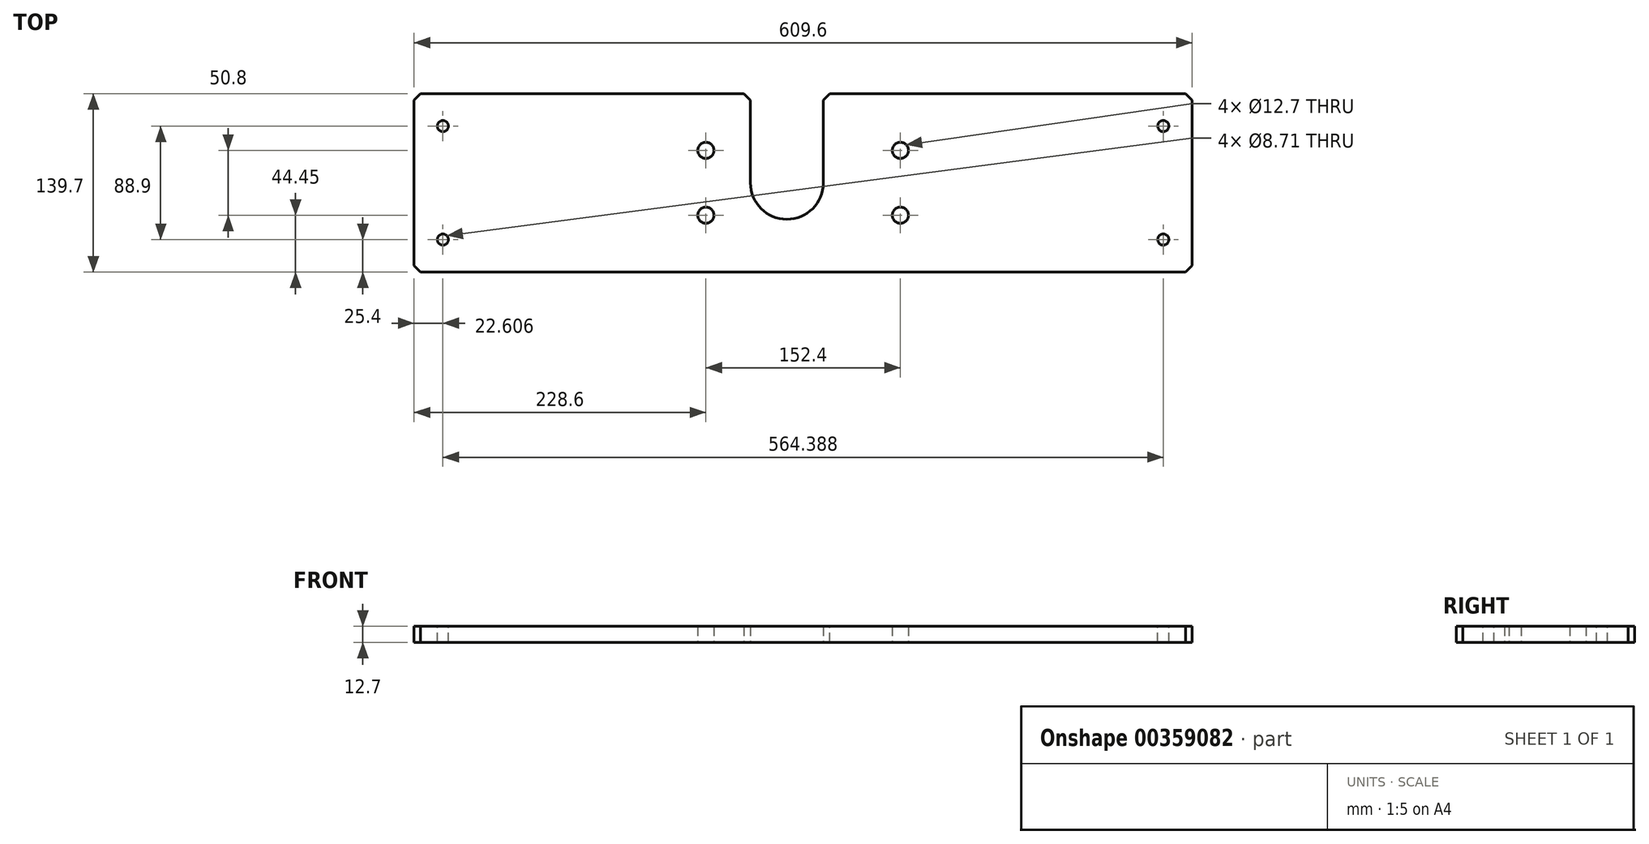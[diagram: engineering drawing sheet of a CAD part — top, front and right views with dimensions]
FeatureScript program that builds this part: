
annotation { "Feature Type Name" : "Feature", "Feature Type Description" : "" }
export const myFeature = defineFeature(function(context is Context, id is Id, definition is map)
    precondition{}
    {
        {
            var Q0;
            Q0=qCreatedBy(makeId("Top.planeOp"),FACE);
            var sketch = newSketch(context, id + "F0", { "sketchPlane" : qUnion([Q0])});
            skLineSegment(sketch, "E0.bottom", {"start": v(0, 0) * mm, "end": v(609.6, 0) * mm});
            skLineSegment(sketch, "E0.top", {"start": v(0, 139.7) * mm, "end": v(263.52, 139.7) * mm});
            skLineSegment(sketch, "E0.left", {"start": v(0, 0) * mm, "end": v(0, 139.7) * mm});
            skLineSegment(sketch, "E0.right", {"start": v(609.6, 0) * mm, "end": v(609.6, 139.7) * mm});
            skLineSegment(sketch, "E1", {"start": v(304.8, 139.7) * mm, "end": v(304.8, 0) * mm, "construction": true});
            skLineSegment(sketch, "E2.bottom", {"start": v(381, 95.25) * mm, "end": v(228.6, 95.25) * mm, "construction": true});
            skLineSegment(sketch, "E2.top", {"start": v(381, 44.45) * mm, "end": v(228.6, 44.45) * mm, "construction": true});
            skLineSegment(sketch, "E2.left", {"start": v(381, 95.25) * mm, "end": v(381, 44.45) * mm, "construction": true});
            skLineSegment(sketch, "E2.right", {"start": v(228.6, 95.25) * mm, "end": v(228.6, 44.45) * mm, "construction": true});
            skPoint(sketch, "E2.middle", {"position": v(304.8, 69.85) * mm});
            skCircle(sketch, "E3", {"center": v(228.6, 95.25) * mm, "radius": 6.35 * mm});
            skCircle(sketch, "E4", {"center": v(381, 95.25) * mm, "radius": 6.35 * mm});
            skCircle(sketch, "E5", {"center": v(381, 44.45) * mm, "radius": 6.35 * mm});
            skCircle(sketch, "E6", {"center": v(228.6, 44.45) * mm, "radius": 6.35 * mm});
            skLineSegment(sketch, "E7.trimOffspring", {"start": v(333.38, 139.7) * mm, "end": v(609.6, 139.7) * mm});
            skArc(sketch, "E8", {"start": v(305.2, 95.25) * mm, "mid": v(305, 95.35) * mm, "end": v(304.8, 95.45) * mm});
            skLineSegment(sketch, "E9", {"start": v(263.52, 69.85) * mm, "end": v(263.52, 139.7) * mm});
            skLineSegment(sketch, "E10", {"start": v(320.68, 69.85) * mm, "end": v(320.68, 139.7) * mm});
            skLineSegment(sketch, "E11.trimOffspring", {"start": v(320.68, 139.7) * mm, "end": v(333.38, 139.7) * mm});
            skArc(sketch, "E12.trimOffspring", {"start": v(263.53, 69.85) * mm, "mid": v(292.1, 41.28) * mm, "end": v(320.68, 69.85) * mm});
            skSolve(sketch);
        }
        {
            var Q0;
            Q0 = qSketchRegion(id + "F0", true);
            extrude(context, id + "F1", {"entities" : qUnion([Q0]), "depth" : 12.7 * mm});
        }
        {
            var Q0;
            Q0=makeQuery(id+"F1.opExtrude","SWEPT_EDGE",EDGE,{"disambiguationData":[OSD([sQuery(id+"F0.wireOp",EDGE,"E0.top"),sQuery(id+"F0.wireOp",EDGE,"E0.right")])]});
            var Q1;
            Q1=makeQuery(id+"F1.opExtrude","SWEPT_EDGE",EDGE,{"disambiguationData":[OSD([sQuery(id+"F0.wireOp",EDGE,"E10"),sQuery(id+"F0.wireOp",EDGE,"E11.trimOffspring")])]});
            var Q2;
            Q2=makeQuery(id+"F1.opExtrude","SWEPT_EDGE",EDGE,{"disambiguationData":[OSD([sQuery(id+"F0.wireOp",EDGE,"E0.bottom"),sQuery(id+"F0.wireOp",EDGE,"E0.left")])]});
            chamfer(context, id + "F2", {"entities" : qUnion([Q0, Q1, Q2]), "width" : 5.08 * mm, "tangentPropagation" : true});
        }
        {
            var Q0;
            Q0=makeQuery(id+"F1.opExtrude","CAP_FACE",FACE,{"disambiguationData":[OSD([sQuery(id+"F0.wireOp",EDGE,"E0.bottom"),sQuery(id+"F0.wireOp",EDGE,"E0.top"),sQuery(id+"F0.wireOp",EDGE,"E0.left"),sQuery(id+"F0.wireOp",EDGE,"E0.right"),sQuery(id+"F0.wireOp",EDGE,"E3"),sQuery(id+"F0.wireOp",EDGE,"E4"),sQuery(id+"F0.wireOp",EDGE,"E5"),sQuery(id+"F0.wireOp",EDGE,"E6"),sQuery(id+"F0.wireOp",EDGE,"E7.trimOffspring"),sQuery(id+"F0.wireOp",EDGE,"E9"),sQuery(id+"F0.wireOp",EDGE,"E10"),sQuery(id+"F0.wireOp",EDGE,"E11.trimOffspring"),sQuery(id+"F0.wireOp",EDGE,"E12.trimOffspring")])],"isStart":false});
            var sketch = newSketch(context, id + "F3", { "sketchPlane" : qUnion([Q0])});
            skLineSegment(sketch, "E13.bottom", {"start": v(22.6, 114.3) * mm, "end": v(587, 114.3) * mm, "construction": true});
            skLineSegment(sketch, "E13.top", {"start": v(22.6, 25.4) * mm, "end": v(587, 25.4) * mm, "construction": true});
            skLineSegment(sketch, "E13.left", {"start": v(22.6, 114.3) * mm, "end": v(22.6, 25.4) * mm, "construction": true});
            skLineSegment(sketch, "E13.right", {"start": v(587, 114.3) * mm, "end": v(587, 25.4) * mm, "construction": true});
            skCircle(sketch, "E14", {"center": v(22.6, 114.3) * mm, "radius": 4.36 * mm});
            skCircle(sketch, "E15", {"center": v(22.6, 25.4) * mm, "radius": 4.36 * mm});
            skCircle(sketch, "E16", {"center": v(587, 114.3) * mm, "radius": 4.36 * mm});
            skCircle(sketch, "E17", {"center": v(587, 25.4) * mm, "radius": 4.36 * mm});
            skLineSegment(sketch, "E18", {"start": v(304.8, 0) * mm, "end": v(304.8, 139.7) * mm, "construction": true});
            skSolve(sketch);
        }
        {
            var Q0;
            Q0=makeQuery(id+"F3.imprint","IMPRINT",FACE,{"disambiguationData":[TD([[makeQuery(id+"F3.imprint","IMPRINT",EDGE,{"derivedFrom":sQuery(id+"F3.wireOp",EDGE,"E14")}),1.0]])]});
            var Q1;
            Q1=makeQuery(id+"F3.imprint","IMPRINT",FACE,{"disambiguationData":[TD([[makeQuery(id+"F3.imprint","IMPRINT",EDGE,{"derivedFrom":sQuery(id+"F3.wireOp",EDGE,"E15")}),1.0]])]});
            var Q2;
            Q2=makeQuery(id+"F3.imprint","IMPRINT",FACE,{"disambiguationData":[TD([[makeQuery(id+"F3.imprint","IMPRINT",EDGE,{"derivedFrom":sQuery(id+"F3.wireOp",EDGE,"E17")}),1.0]])]});
            var Q3;
            Q3=makeQuery(id+"F3.imprint","IMPRINT",FACE,{"disambiguationData":[TD([[makeQuery(id+"F3.imprint","IMPRINT",EDGE,{"derivedFrom":sQuery(id+"F3.wireOp",EDGE,"E16")}),1.0]])]});
            extrude(context, id + "F4", {"entities" : qUnion([Q0, Q1, Q2, Q3]), "operationType" : NewBodyOperationType.REMOVE, "endBound" : BoundingType.THROUGH_ALL, "oppositeDirection" : true, "depth" : 25.4 * mm});
        }
    });
